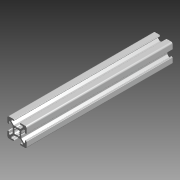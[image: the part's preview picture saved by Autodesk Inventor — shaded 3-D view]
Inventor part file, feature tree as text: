
AUTODESK INVENTOR PART (.ipt)
format: ipt  version: 2013 (Build 170138000, 138)  size: 284,672 bytes
history: native  units: in
note: dims shown in document units (in); Inventor stores cm internally (conversion verified against a paired STEP export)
features: other x3, extrude x1, sketch x1
ambient origin geometry x8: Origin, YZ Plane, XZ Plane, XY Plane, X Axis, Y Axis, Z Axis, Center Point
bodies: Solid1 (feature_tree)
feature tree (5):
  other  "Blocks"
  extrude  "Extrusion1"  [1 undecoded]
  sketch  "Sketch1"  dims[d1=0.0in]
  other  "20x20"
  other  "20x20:1"
note: 1 required parameter value undecoded (feature->parameter linkage not recoverable at this tier; creation-order binding heuristic only, values carry confidence <= 0.55)
